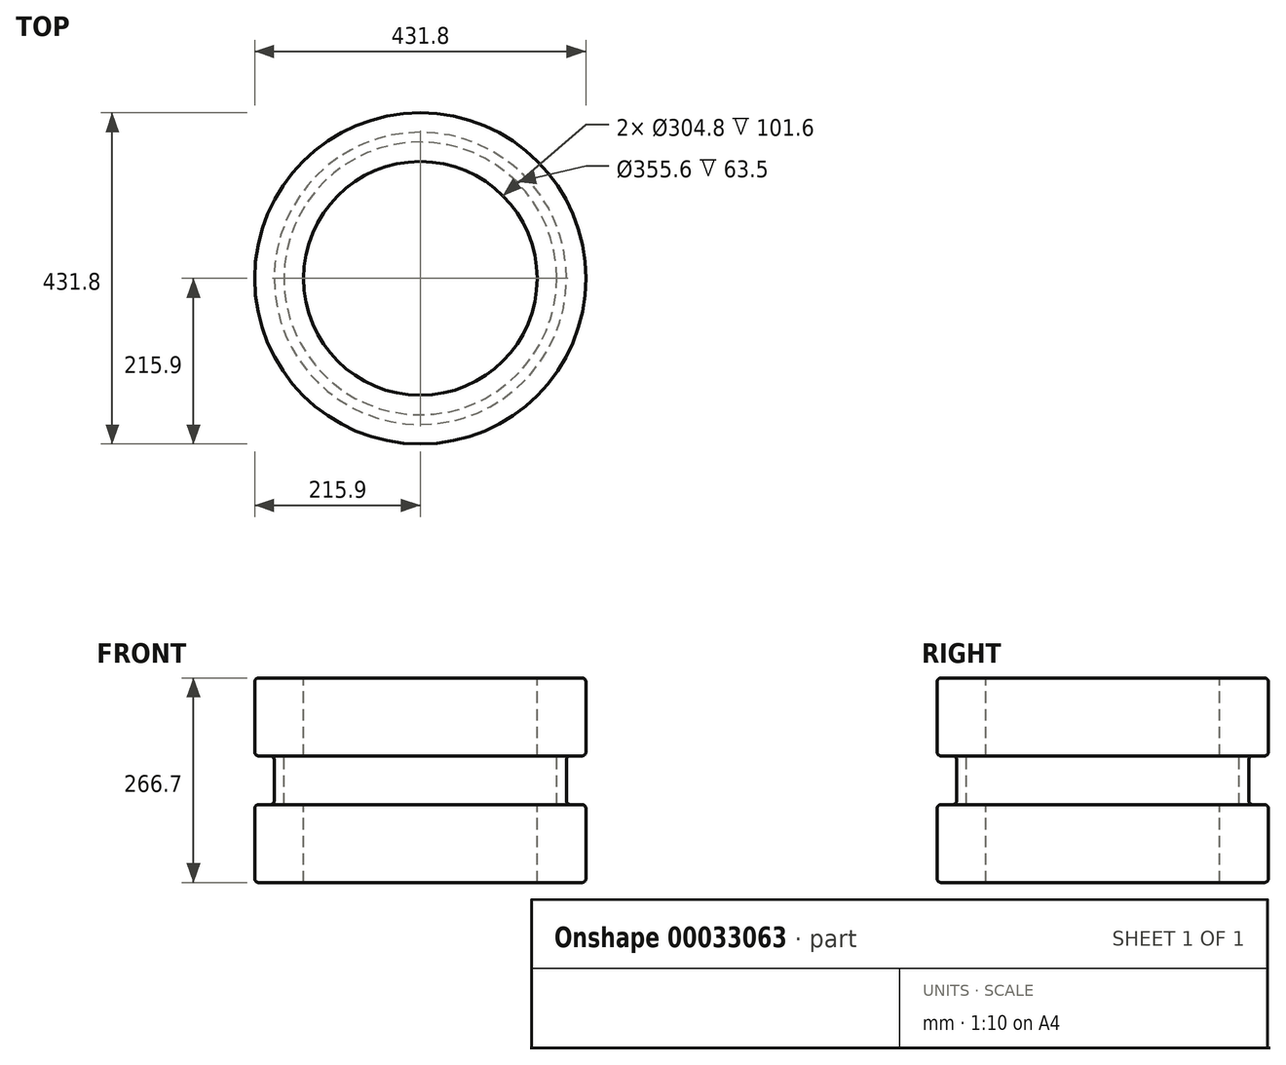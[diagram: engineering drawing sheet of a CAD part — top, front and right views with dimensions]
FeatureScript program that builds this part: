
annotation { "Feature Type Name" : "Feature", "Feature Type Description" : "" }
export const myFeature = defineFeature(function(context is Context, id is Id, definition is map)
    precondition{}
    {
        {
            var Q0;
            Q0=qCreatedBy(makeId("Front.planeOp"),FACE);
            var sketch = newSketch(context, id + "F0", { "sketchPlane" : qUnion([Q0])});
            skLineSegment(sketch, "E0.bottom", {"start": v(0, 0) * mm, "end": v(-25.4, 0) * mm});
            skLineSegment(sketch, "E0.top", {"start": v(0, 101.6) * mm, "end": v(-63.5, 101.6) * mm});
            skLineSegment(sketch, "E0.left", {"start": v(0, 0) * mm, "end": v(0, 101.6) * mm});
            skLineSegment(sketch, "E0.right", {"start": v(-63.5, 0) * mm, "end": v(-63.5, 101.6) * mm});
            skLineSegment(sketch, "E1.left", {"start": v(-25.4, 0) * mm, "end": v(-25.4, -63.5) * mm});
            skLineSegment(sketch, "E1.right", {"start": v(-38.1, 0) * mm, "end": v(-38.1, -63.5) * mm});
            skPoint(sketch, "E2.firstSnap0", {"position": v(-31.75, -63.5) * mm});
            skLineSegment(sketch, "E2.bottom", {"start": v(0, -63.5) * mm, "end": v(-25.4, -63.5) * mm});
            skLineSegment(sketch, "E2.top", {"start": v(0, -165.1) * mm, "end": v(-63.5, -165.1) * mm});
            skLineSegment(sketch, "E2.left", {"start": v(0, -63.5) * mm, "end": v(0, -165.1) * mm});
            skLineSegment(sketch, "E2.right", {"start": v(-63.5, -63.5) * mm, "end": v(-63.5, -165.1) * mm});
            skLineSegment(sketch, "E3", {"start": v(152.4, 170.91) * mm, "end": v(152.4, -210.09) * mm});
            skLineSegment(sketch, "E4.trimOffspring", {"start": v(-38.1, -63.5) * mm, "end": v(-63.5, -63.5) * mm});
            skLineSegment(sketch, "E5.trimOffspring", {"start": v(-38.1, 0) * mm, "end": v(-63.5, 0) * mm});
            skSolve(sketch);
        }
        {
            var Q0;
            Q0 = qSketchRegion(id + "F0", true);
            var Q1;
            Q1=sQuery(id+"F0.wireOp",EDGE,"E3");
            revolve(context, id + "F1", {"entities" : qUnion([Q0]), "axis" : qUnion([Q1]), "revolveType" : RevolveType.FULL});
        }
        {
            var Q0;
            Q0=makeQuery(id+"F1.opRevolve","SWEPT_FACE",FACE,{"disambiguationData":[OSD([sQuery(id+"F0.wireOp",EDGE,"E1.right")])]});
            var Q1;
            Q1=makeQuery(id+"F1.opRevolve","SWEPT_FACE",FACE,{"disambiguationData":[OSD([sQuery(id+"F0.wireOp",EDGE,"E0.right")])]});
            var Q2;
            Q2=makeQuery(id+"F1.opRevolve","SWEPT_FACE",FACE,{"disambiguationData":[OSD([sQuery(id+"F0.wireOp",EDGE,"E2.right")])]});
            fillet(context, id + "F2", {"entities" : qUnion([Q0, Q1, Q2]), "radius" : 5.08 * mm, "tangentPropagation" : true, "allowEdgeOverflow" : false});
        }
    });
